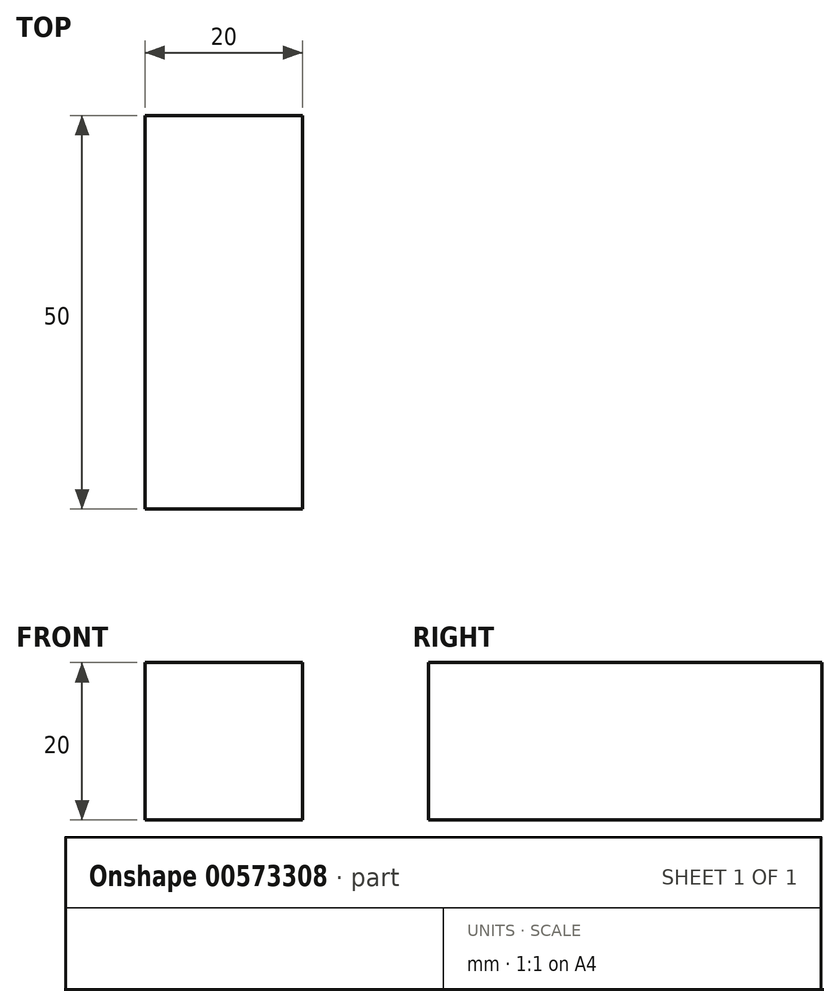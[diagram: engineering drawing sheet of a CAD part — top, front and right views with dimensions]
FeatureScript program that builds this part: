
annotation { "Feature Type Name" : "Feature", "Feature Type Description" : "" }
export const myFeature = defineFeature(function(context is Context, id is Id, definition is map)
    precondition{}
    {
        {
            var Q0;
            Q0=qCreatedBy(makeId("Front.planeOp"),FACE);
            var sketch = newSketch(context, id + "F0", { "sketchPlane" : qUnion([Q0])});
            skLineSegment(sketch, "E0.bottom", {"start": v(0, 0) * mm, "end": v(20, 0) * mm});
            skLineSegment(sketch, "E0.top", {"start": v(0, 20) * mm, "end": v(20, 20) * mm});
            skLineSegment(sketch, "E0.left", {"start": v(0, 0) * mm, "end": v(0, 20) * mm});
            skLineSegment(sketch, "E0.right", {"start": v(20, 0) * mm, "end": v(20, 20) * mm});
            skSolve(sketch);
        }
        {
            var Q0;
            Q0=makeQuery(id+"F0.imprint","IMPRINT",FACE,{"disambiguationData":[TD([[makeQuery(id+"F0.imprint","IMPRINT",EDGE,{"derivedFrom":sQuery(id+"F0.wireOp",EDGE,"E0.bottom")}),1.0]])]});
            extrude(context, id + "F1", {"entities" : qUnion([Q0]), "depth" : 50 * mm, "offsetDistance" : 25 * mm});
        }
    });
